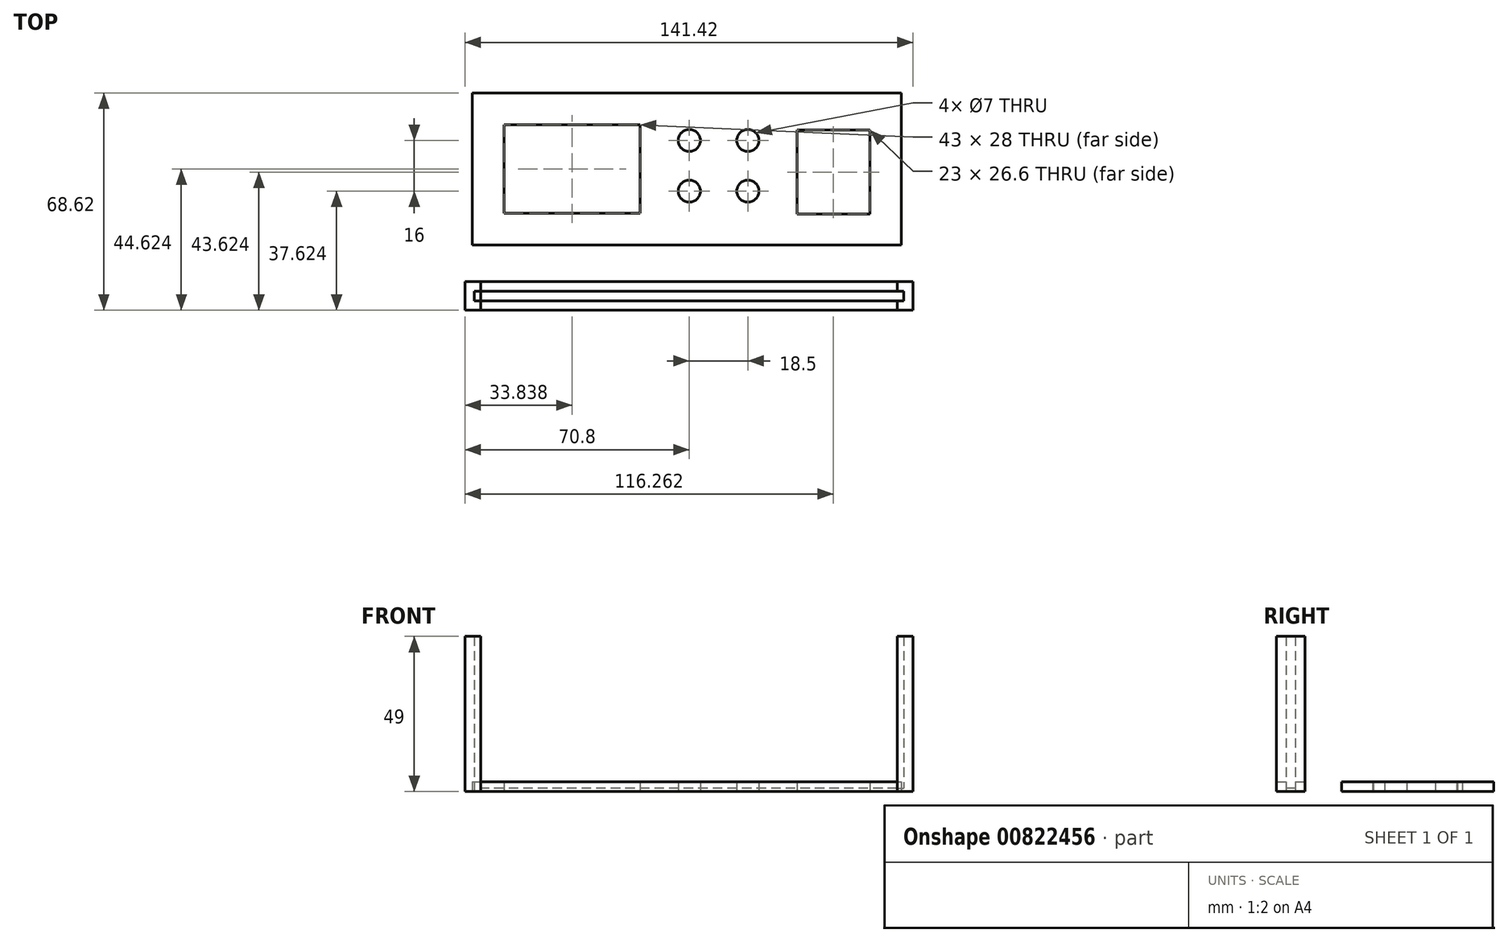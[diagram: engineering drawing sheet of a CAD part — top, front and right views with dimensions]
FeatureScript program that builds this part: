
annotation { "Feature Type Name" : "Feature", "Feature Type Description" : "" }
export const myFeature = defineFeature(function(context is Context, id is Id, definition is map)
    precondition{}
    {
        {
            var Q0;
            Q0=qCreatedBy(makeId("Top.planeOp"),FACE);
            var sketch = newSketch(context, id + "F0", { "sketchPlane" : qUnion([Q0])});
            skLineSegment(sketch, "E0.bottom", {"start": v(-67.71, 26.23) * mm, "end": v(-24.71, 26.23) * mm});
            skLineSegment(sketch, "E0.top", {"start": v(-67.71, -1.77) * mm, "end": v(-24.71, -1.77) * mm});
            skLineSegment(sketch, "E0.left", {"start": v(-67.71, 26.23) * mm, "end": v(-67.71, -1.77) * mm});
            skLineSegment(sketch, "E0.right", {"start": v(-24.71, 26.23) * mm, "end": v(-24.71, -1.77) * mm});
            skLineSegment(sketch, "E1.bottom", {"start": v(-77.71, 36.23) * mm, "end": v(57.71, 36.23) * mm});
            skLineSegment(sketch, "E1.top", {"start": v(-77.71, -11.77) * mm, "end": v(57.71, -11.77) * mm});
            skLineSegment(sketch, "E1.left", {"start": v(-77.71, 36.23) * mm, "end": v(-77.71, -11.77) * mm});
            skLineSegment(sketch, "E1.right", {"start": v(57.71, 36.23) * mm, "end": v(57.71, -11.77) * mm});
            skLineSegment(sketch, "E2", {"start": v(0, 21.23) * mm, "end": v(-9.25, 21.23) * mm, "construction": true});
            skLineSegment(sketch, "E3", {"start": v(0, 21.23) * mm, "end": v(9.25, 21.23) * mm, "construction": true});
            skLineSegment(sketch, "E4", {"start": v(0, 5.23) * mm, "end": v(-9.25, 5.23) * mm, "construction": true});
            skLineSegment(sketch, "E5", {"start": v(0, 5.23) * mm, "end": v(9.25, 5.23) * mm, "construction": true});
            skCircle(sketch, "E6", {"center": v(-9.25, 21.23) * mm, "radius": 3.5 * mm});
            skCircle(sketch, "E7", {"center": v(9.25, 21.23) * mm, "radius": 3.5 * mm});
            skCircle(sketch, "E8", {"center": v(9.25, 5.23) * mm, "radius": 3.5 * mm});
            skCircle(sketch, "E9", {"center": v(-9.25, 5.23) * mm, "radius": 3.5 * mm});
            skLineSegment(sketch, "E10.bottom", {"start": v(24.71, 24.53) * mm, "end": v(47.71, 24.53) * mm});
            skLineSegment(sketch, "E10.top", {"start": v(24.71, -2.07) * mm, "end": v(47.71, -2.07) * mm});
            skLineSegment(sketch, "E10.left", {"start": v(24.71, 24.53) * mm, "end": v(24.71, -2.07) * mm});
            skLineSegment(sketch, "E10.right", {"start": v(47.71, 24.53) * mm, "end": v(47.71, -2.07) * mm});
            skLineSegment(sketch, "E11", {"start": v(0, 36.23) * mm, "end": v(0, -11.77) * mm, "construction": true});
            skLineSegment(sketch, "E12", {"start": v(-77.05, -26.39) * mm, "end": v(58.37, -26.39) * mm});
            skLineSegment(sketch, "E13", {"start": v(-77.05, -26.39) * mm, "end": v(-77.05, -29.39) * mm});
            skLineSegment(sketch, "E14", {"start": v(58.37, -26.39) * mm, "end": v(58.37, -29.39) * mm});
            skLineSegment(sketch, "E15", {"start": v(58.37, -29.39) * mm, "end": v(-77.05, -29.39) * mm});
            skLineSegment(sketch, "E16", {"start": v(-77.05, -23.39) * mm, "end": v(58.37, -23.39) * mm});
            skLineSegment(sketch, "E17", {"start": v(58.37, -32.39) * mm, "end": v(-77.05, -32.39) * mm});
            skLineSegment(sketch, "E18", {"start": v(-77.05, -32.39) * mm, "end": v(-80.05, -32.39) * mm});
            skLineSegment(sketch, "E19", {"start": v(-80.05, -32.39) * mm, "end": v(-80.05, -23.39) * mm});
            skLineSegment(sketch, "E20", {"start": v(-77.05, -23.39) * mm, "end": v(-80.05, -23.39) * mm});
            skLineSegment(sketch, "E21", {"start": v(-77.05, -32.39) * mm, "end": v(-75.05, -32.39) * mm});
            skLineSegment(sketch, "E22", {"start": v(-75.05, -32.39) * mm, "end": v(-75.05, -23.39) * mm});
            skLineSegment(sketch, "E23", {"start": v(58.37, -23.39) * mm, "end": v(61.37, -23.39) * mm});
            skLineSegment(sketch, "E24", {"start": v(58.37, -32.39) * mm, "end": v(61.37, -32.39) * mm});
            skLineSegment(sketch, "E25", {"start": v(61.37, -32.39) * mm, "end": v(61.37, -23.39) * mm});
            skLineSegment(sketch, "E26", {"start": v(56.37, -32.39) * mm, "end": v(56.37, -29.39) * mm});
            skLineSegment(sketch, "E27", {"start": v(56.37, -26.39) * mm, "end": v(56.37, -23.39) * mm});
            skLineSegment(sketch, "E28", {"start": v(-75.05, -32.39) * mm, "end": v(-75.05, -29.39) * mm});
            skLineSegment(sketch, "E29", {"start": v(-75.05, -26.39) * mm, "end": v(-75.05, -23.39) * mm});
            skSolve(sketch);
        }
        {
            var Q0;
            Q0=makeQuery(id+"F0.imprint","IMPRINT",FACE,{"disambiguationData":[TD([[makeQuery(id+"F0.imprint","IMPRINT",EDGE,{"derivedFrom":sQuery(id+"F0.wireOp",EDGE,"E0.bottom")}),1.0]])]});
            extrude(context, id + "F1", {"entities" : qUnion([Q0]), "depth" : 3 * mm, "offsetDistance" : 25 * mm});
        }
        {
            var Q0;
            {var subQ5=sQuery(id+"F0.wireOp",EDGE,"E14");Q0=makeQuery(id+"F0.imprint","IMPRINT",FACE,{"disambiguationData":[TD([[makeQuery(id+"F0.imprint","IMPRINT",EDGE,{"derivedFrom":subQ5}),1.0]])]});}
            var Q1;
            {var subQ1=sQuery(id+"F0.wireOp",EDGE,"E13");Q1=makeQuery(id+"F0.imprint","IMPRINT",FACE,{"disambiguationData":[TD([[makeQuery(id+"F0.imprint","IMPRINT",EDGE,{"derivedFrom":subQ1}),-1.0]])]});}
            extrude(context, id + "F2", {"entities" : qUnion([Q0, Q1]), "depth" : 49 * mm, "offsetDistance" : 25 * mm});
        }
        {
            var Q0;
            {var subQ1=sQuery(id+"F0.wireOp",EDGE,"E14");Q0=makeQuery(id+"F0.imprint","IMPRINT",FACE,{"disambiguationData":[TD([[makeQuery(id+"F0.imprint","IMPRINT",EDGE,{"derivedFrom":subQ1}),-1.0]])]});}
            extrude(context, id + "F3", {"entities" : qUnion([Q0]), "operationType" : NewBodyOperationType.ADD, "depth" : 1 * mm, "offsetDistance" : 25 * mm});
        }
        {
            var Q0;
            {var subQ2=sQuery(id+"F0.wireOp",EDGE,"E26");Q0=makeQuery(id+"F0.imprint","IMPRINT",FACE,{"disambiguationData":[TD([[makeQuery(id+"F0.imprint","IMPRINT",EDGE,{"derivedFrom":subQ2}),1.0]])]});}
            var Q1;
            {var subQ2=sQuery(id+"F0.wireOp",EDGE,"E27");Q1=makeQuery(id+"F0.imprint","IMPRINT",FACE,{"disambiguationData":[TD([[makeQuery(id+"F0.imprint","IMPRINT",EDGE,{"derivedFrom":subQ2}),1.0]])]});}
            extrude(context, id + "F4", {"entities" : qUnion([Q0, Q1]), "depth" : 3 * mm, "offsetDistance" : 25 * mm});
        }
    });
